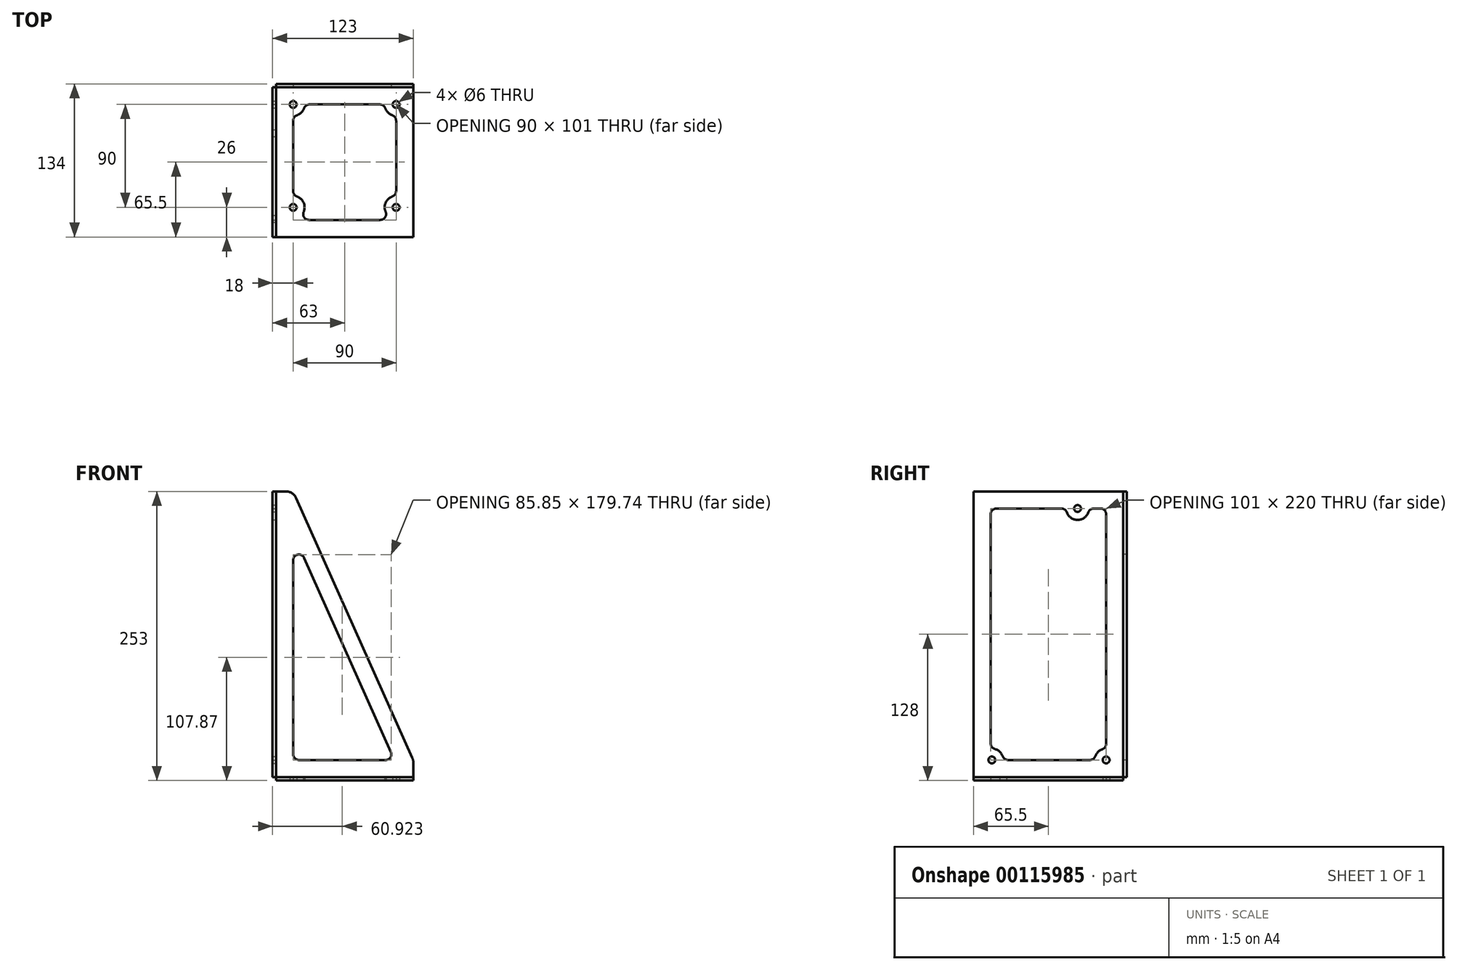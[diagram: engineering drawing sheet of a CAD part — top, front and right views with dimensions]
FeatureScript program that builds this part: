
annotation { "Feature Type Name" : "Feature", "Feature Type Description" : "" }
export const myFeature = defineFeature(function(context is Context, id is Id, definition is map)
    precondition{}
    {
        {
            var Q0;
            Q0=qCreatedBy(makeId("Top.planeOp"),FACE);
            var sketch = newSketch(context, id + "F0", { "sketchPlane" : qUnion([Q0])});
            skCircle(sketch, "E0", {"center": v(0, 0) * mm, "radius": 3 * mm});
            skCircle(sketch, "E1", {"center": v(0, 90) * mm, "radius": 3 * mm});
            skCircle(sketch, "E2", {"center": v(90, 0) * mm, "radius": 3 * mm});
            skCircle(sketch, "E3", {"center": v(90, 90) * mm, "radius": 3 * mm});
            skArc(sketch, "E4", {"start": v(3.33, 80.57) * mm, "mid": v(7.07, 82.93) * mm, "end": v(9.43, 86.67) * mm});
            skArc(sketch, "E5", {"start": v(80.57, 86.67) * mm, "mid": v(82.93, 82.93) * mm, "end": v(86.67, 80.57) * mm});
            skArc(sketch, "E6", {"start": v(86.67, 9.43) * mm, "mid": v(80.83, 3.98) * mm, "end": v(80.83, -4) * mm});
            skArc(sketch, "E7", {"start": v(9.17, -4) * mm, "mid": v(9.17, 3.98) * mm, "end": v(3.33, 9.43) * mm});
            skLineSegment(sketch, "E8.bottom", {"start": v(-15, 105) * mm, "end": v(105, 105) * mm});
            skLineSegment(sketch, "E8.top", {"start": v(-15, -26) * mm, "end": v(105, -26) * mm});
            skLineSegment(sketch, "E8.left", {"start": v(-15, 105) * mm, "end": v(-15, -26) * mm});
            skLineSegment(sketch, "E8.right", {"start": v(105, 105) * mm, "end": v(105, -26) * mm});
            skLineSegment(sketch, "E9", {"start": v(0, 75.86) * mm, "end": v(0, 14.14) * mm});
            skLineSegment(sketch, "E10", {"start": v(13.75, -11) * mm, "end": v(76.25, -11) * mm});
            skLineSegment(sketch, "E11", {"start": v(90, 14.14) * mm, "end": v(90, 75.86) * mm});
            skLineSegment(sketch, "E12", {"start": v(75.86, 90) * mm, "end": v(14.14, 90) * mm});
            skPoint(sketch, "E13.orphan", {"position": v(0, 80) * mm});
            skPoint(sketch, "E14.orphan", {"position": v(80, 90) * mm});
            skPoint(sketch, "E15.orphan", {"position": v(90, 10) * mm});
            skPoint(sketch, "E16.orphan", {"position": v(0, -10) * mm});
            skArc(sketch, "E17.filletArc", {"start": v(3.33, 80.57) * mm, "mid": v(0.92, 78.74) * mm, "end": v(0, 75.86) * mm});
            skPoint(sketch, "E18.visualSharp", {"position": v(10, 90) * mm});
            skArc(sketch, "E18.filletArc", {"start": v(14.14, 90) * mm, "mid": v(11.26, 89.08) * mm, "end": v(9.43, 86.67) * mm});
            skArc(sketch, "E19.filletArc", {"start": v(80.57, 86.67) * mm, "mid": v(78.74, 89.08) * mm, "end": v(75.86, 90) * mm});
            skPoint(sketch, "E20.visualSharp", {"position": v(90, 80) * mm});
            skArc(sketch, "E20.filletArc", {"start": v(90, 75.86) * mm, "mid": v(89.08, 78.74) * mm, "end": v(86.67, 80.57) * mm});
            skArc(sketch, "E21.filletArc", {"start": v(86.67, 9.43) * mm, "mid": v(89.08, 11.26) * mm, "end": v(90, 14.14) * mm});
            skPoint(sketch, "E22.visualSharp", {"position": v(0, 10) * mm});
            skArc(sketch, "E22.filletArc", {"start": v(0, 14.14) * mm, "mid": v(0.92, 11.26) * mm, "end": v(3.33, 9.43) * mm});
            skArc(sketch, "E23", {"start": v(9.17, -4) * mm, "mid": v(9.56, -8.74) * mm, "end": v(13.75, -11) * mm});
            skArc(sketch, "E24", {"start": v(76.25, -11) * mm, "mid": v(80.44, -8.74) * mm, "end": v(80.83, -4) * mm});
            skPoint(sketch, "E25.start.orphan", {"position": v(90, -11) * mm});
            skSolve(sketch);
        }
        {
            var Q0;
            Q0=qSketchRegion(id+"F0",true);
            extrude(context, id + "F1", {"entities" : qUnion([Q0]), "depth" : 3 * mm});
        }
        {
            var Q0;
            Q0=makeQuery(id+"F1.opExtrude","SWEPT_FACE",FACE,{"disambiguationData":[OSD([sQuery(id+"F0.wireOp",EDGE,"E8.left")])]});
            var sketch = newSketch(context, id + "F2", { "sketchPlane" : qUnion([Q0])});
            skLineSegment(sketch, "E26.0", {"start": v(-105, 3) * mm, "end": v(26, 3) * mm});
            skCircle(sketch, "E27", {"center": v(-90, 18) * mm, "radius": 3 * mm});
            skCircle(sketch, "E28", {"center": v(10, 18) * mm, "radius": 3 * mm});
            skCircle(sketch, "E29", {"center": v(-65, 238) * mm, "radius": 3 * mm});
            skLineSegment(sketch, "E30.top", {"start": v(-105, 253) * mm, "end": v(26, 253) * mm});
            skLineSegment(sketch, "E30.left", {"start": v(-105, 3) * mm, "end": v(-105, 253) * mm});
            skLineSegment(sketch, "E30.right", {"start": v(26, 3) * mm, "end": v(26, 253) * mm});
            skArc(sketch, "E31", {"start": v(-74.43, 234.67) * mm, "mid": v(-65, 228) * mm, "end": v(-55.57, 234.67) * mm});
            skArc(sketch, "E32", {"start": v(-80.57, 21.33) * mm, "mid": v(-82.93, 25.07) * mm, "end": v(-86.67, 27.43) * mm});
            skArc(sketch, "E33", {"start": v(7.33, 27.64) * mm, "mid": v(3.18, 25.31) * mm, "end": v(0.57, 21.33) * mm});
            skLineSegment(sketch, "E34", {"start": v(-90, 32.14) * mm, "end": v(-90, 233) * mm});
            skLineSegment(sketch, "E35", {"start": v(-85, 238) * mm, "end": v(-79.14, 238) * mm});
            skLineSegment(sketch, "E36", {"start": v(-4.14, 18) * mm, "end": v(-75.86, 18) * mm});
            skPoint(sketch, "E37.orphan", {"position": v(-90, 28) * mm});
            skPoint(sketch, "E38.orphan", {"position": v(0, 18) * mm});
            skLineSegment(sketch, "E39", {"start": v(-50.86, 238) * mm, "end": v(6, 238) * mm});
            skLineSegment(sketch, "E40", {"start": v(11, 233) * mm, "end": v(11, 32.46) * mm});
            skPoint(sketch, "E41.orphan", {"position": v(-55, 238) * mm});
            skPoint(sketch, "E42.visualSharp", {"position": v(-90, 238) * mm});
            skArc(sketch, "E42.filletArc", {"start": v(-85, 238) * mm, "mid": v(-88.54, 236.54) * mm, "end": v(-90, 233) * mm});
            skPoint(sketch, "E43.visualSharp", {"position": v(-75, 238) * mm});
            skArc(sketch, "E43.filletArc", {"start": v(-74.43, 234.67) * mm, "mid": v(-76.26, 237.08) * mm, "end": v(-79.14, 238) * mm});
            skArc(sketch, "E44.filletArc", {"start": v(-50.86, 238) * mm, "mid": v(-53.74, 237.08) * mm, "end": v(-55.57, 234.67) * mm});
            skPoint(sketch, "E45.visualSharp", {"position": v(11, 238) * mm});
            skArc(sketch, "E45.filletArc", {"start": v(11, 233) * mm, "mid": v(9.54, 236.54) * mm, "end": v(6, 238) * mm});
            skPoint(sketch, "E46.visualSharp", {"position": v(11, 27.95) * mm});
            skArc(sketch, "E46.filletArc", {"start": v(7.33, 27.64) * mm, "mid": v(9.98, 29.43) * mm, "end": v(11, 32.46) * mm});
            skArc(sketch, "E47.filletArc", {"start": v(-4.14, 18) * mm, "mid": v(-1.26, 18.92) * mm, "end": v(0.57, 21.33) * mm});
            skPoint(sketch, "E48.visualSharp", {"position": v(-80, 18) * mm});
            skArc(sketch, "E48.filletArc", {"start": v(-80.57, 21.33) * mm, "mid": v(-78.74, 18.92) * mm, "end": v(-75.86, 18) * mm});
            skArc(sketch, "E49.filletArc", {"start": v(-90, 32.14) * mm, "mid": v(-89.08, 29.26) * mm, "end": v(-86.67, 27.43) * mm});
            skSolve(sketch);
        }
        {
            var Q0;
            Q0=qSketchRegion(id+"F2",true);
            extrude(context, id + "F3", {"entities" : qUnion([Q0]), "depth" : 3 * mm});
        }
        {
            var Q0;
            Q0=makeQuery(id+"F1.opExtrude","SWEPT_FACE",FACE,{"disambiguationData":[OSD([sQuery(id+"F0.wireOp",EDGE,"E8.bottom")])]});
            var sketch = newSketch(context, id + "F4", { "sketchPlane" : qUnion([Q0])});
            skLineSegment(sketch, "E50.0", {"start": v(15, 3) * mm, "end": v(-105, 3) * mm});
            skLineSegment(sketch, "E51.0", {"start": v(15, 3) * mm, "end": v(15, 253) * mm});
            skLineSegment(sketch, "E52", {"start": v(15, 253) * mm, "end": v(6.48, 253) * mm});
            skLineSegment(sketch, "E53", {"start": v(-2.65, 247.08) * mm, "end": v(-104.13, 19.95) * mm});
            skLineSegment(sketch, "E54", {"start": v(-105, 15.87) * mm, "end": v(-105, 3) * mm});
            skPoint(sketch, "E55.visualSharp", {"position": v(0, 253) * mm});
            skArc(sketch, "E55.filletArc", {"start": v(6.48, 253) * mm, "mid": v(1.04, 251.4) * mm, "end": v(-2.65, 247.08) * mm});
            skPoint(sketch, "E56.visualSharp", {"position": v(-105, 18) * mm});
            skArc(sketch, "E56.filletArc", {"start": v(-104.13, 19.95) * mm, "mid": v(-104.78, 17.95) * mm, "end": v(-105, 15.87) * mm});
            skLineSegment(sketch, "E57", {"start": v(0, 192.78) * mm, "end": v(0, 23) * mm});
            skLineSegment(sketch, "E58", {"start": v(-5, 18) * mm, "end": v(-80.86, 18) * mm});
            skLineSegment(sketch, "E59", {"start": v(-85.43, 25.04) * mm, "end": v(-9.57, 194.82) * mm});
            skPoint(sketch, "E60.visualSharp", {"position": v(0, 216.23) * mm});
            skArc(sketch, "E60.filletArc", {"start": v(0, 192.78) * mm, "mid": v(-3.96, 197.67) * mm, "end": v(-9.57, 194.82) * mm});
            skPoint(sketch, "E61.visualSharp", {"position": v(-88.57, 18) * mm});
            skArc(sketch, "E61.filletArc", {"start": v(-85.43, 25.04) * mm, "mid": v(-85.06, 20.28) * mm, "end": v(-80.86, 18) * mm});
            skPoint(sketch, "E62.visualSharp", {"position": v(0, 18) * mm});
            skArc(sketch, "E62.filletArc", {"start": v(-5, 18) * mm, "mid": v(-1.46, 19.46) * mm, "end": v(0, 23) * mm});
            skSolve(sketch);
        }
        {
            var Q0;
            Q0=qSketchRegion(id+"F4",true);
            extrude(context, id + "F5", {"entities" : qUnion([Q0]), "depth" : 3 * mm});
        }
    });
